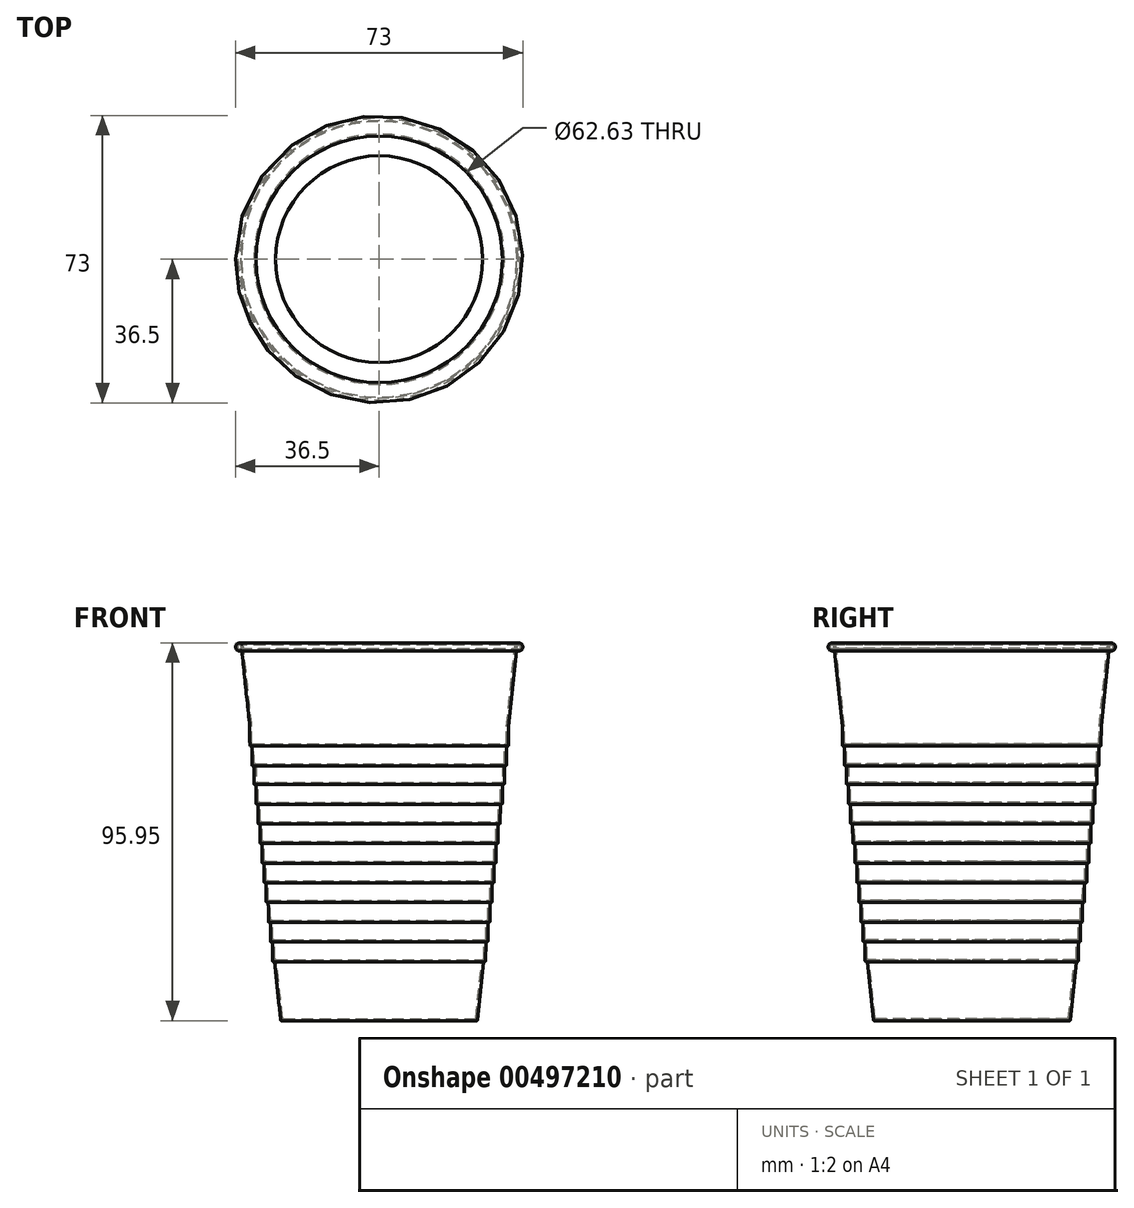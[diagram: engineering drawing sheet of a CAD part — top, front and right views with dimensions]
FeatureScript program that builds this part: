
annotation { "Feature Type Name" : "Feature", "Feature Type Description" : "" }
export const myFeature = defineFeature(function(context is Context, id is Id, definition is map)
    precondition{}
    {
        {
            var Q0;
            Q0=qCreatedBy(makeId("Front.planeOp"),FACE);
            var sketch = newSketch(context, id + "F0", { "sketchPlane" : qUnion([Q0])});
            skLineSegment(sketch, "E0", {"start": v(0, 0) * mm, "end": v(24.82, 0) * mm});
            skLineSegment(sketch, "E1", {"start": v(25.02, 0.18) * mm, "end": v(26.56, 14.82) * mm});
            skLineSegment(sketch, "E2", {"start": v(26.76, 15) * mm, "end": v(26.88, 15) * mm});
            skLineSegment(sketch, "E3", {"start": v(27.08, 15.2) * mm, "end": v(27.1, 19.8) * mm});
            skLineSegment(sketch, "E4", {"start": v(27.3, 20) * mm, "end": v(27.4, 20) * mm});
            skLineSegment(sketch, "E5", {"start": v(27.6, 20.2) * mm, "end": v(27.63, 24.8) * mm});
            skLineSegment(sketch, "E6", {"start": v(27.83, 25) * mm, "end": v(27.93, 25) * mm});
            skLineSegment(sketch, "E7", {"start": v(28.13, 25.2) * mm, "end": v(28.16, 29.8) * mm});
            skLineSegment(sketch, "E8", {"start": v(28.36, 30) * mm, "end": v(28.46, 30) * mm});
            skLineSegment(sketch, "E9", {"start": v(28.66, 30.2) * mm, "end": v(28.68, 34.8) * mm});
            skLineSegment(sketch, "E10", {"start": v(29.19, 35.2) * mm, "end": v(29.2, 39.8) * mm});
            skLineSegment(sketch, "E11", {"start": v(28.88, 35) * mm, "end": v(28.99, 35) * mm});
            skLineSegment(sketch, "E12", {"start": v(29.4, 40) * mm, "end": v(29.51, 40) * mm});
            skLineSegment(sketch, "E13", {"start": v(29.71, 40.2) * mm, "end": v(29.74, 44.8) * mm});
            skLineSegment(sketch, "E14", {"start": v(29.94, 45) * mm, "end": v(30.04, 45) * mm});
            skLineSegment(sketch, "E15", {"start": v(30.24, 45.2) * mm, "end": v(30.26, 49.8) * mm});
            skLineSegment(sketch, "E16", {"start": v(30.46, 50) * mm, "end": v(30.56, 50) * mm});
            skLineSegment(sketch, "E17", {"start": v(30.76, 50.2) * mm, "end": v(30.79, 54.8) * mm});
            skLineSegment(sketch, "E18", {"start": v(30.99, 55) * mm, "end": v(31.1, 55) * mm});
            skLineSegment(sketch, "E19", {"start": v(31.3, 55.2) * mm, "end": v(31.31, 59.8) * mm});
            skLineSegment(sketch, "E20", {"start": v(31.51, 60) * mm, "end": v(31.62, 60) * mm});
            skLineSegment(sketch, "E21", {"start": v(31.82, 60.2) * mm, "end": v(31.82, 64.55) * mm});
            skLineSegment(sketch, "E22", {"start": v(32.02, 64.75) * mm, "end": v(32.12, 64.75) * mm});
            skLineSegment(sketch, "E23", {"start": v(32.32, 64.95) * mm, "end": v(32.34, 69.55) * mm});
            skLineSegment(sketch, "E24", {"start": v(32.54, 69.75) * mm, "end": v(32.64, 69.75) * mm});
            skLineSegment(sketch, "E25", {"start": v(32.84, 69.95) * mm, "end": v(32.87, 74.74) * mm});
            skArc(sketch, "E26", {"start": v(35.25, 94.51) * mm, "mid": v(35.94, 95.17) * mm, "end": v(35, 95) * mm});
            skLineSegment(sketch, "E27", {"start": v(35.25, 94.51) * mm, "end": v(35.5, 94.95) * mm, "construction": true});
            skLineSegment(sketch, "E28", {"start": v(35.5, 94.95) * mm, "end": v(35.5, 94.45) * mm, "construction": true});
            skArc(sketch, "E29.0", {"start": v(35, 94.08) * mm, "mid": v(36.39, 95.4) * mm, "end": v(34.5, 95.05) * mm});
            skLineSegment(sketch, "E29.2", {"start": v(0, 0.5) * mm, "end": v(24.37, 0.5) * mm});
            skLineSegment(sketch, "E30", {"start": v(35, 94.08) * mm, "end": v(35.25, 94.51) * mm});
            skLineSegment(sketch, "E31", {"start": v(0, 0.5) * mm, "end": v(0, 0) * mm});
            skLineSegment(sketch, "E32", {"start": v(0, 0.5) * mm, "end": v(0, 74.17) * mm, "construction": true});
            skLineSegment(sketch, "E33.trimOffspring", {"start": v(32.87, 74.76) * mm, "end": v(35, 95) * mm});
            skLineSegment(sketch, "E34.0", {"start": v(32.35, 70.45) * mm, "end": v(32.37, 74.77) * mm});
            skLineSegment(sketch, "E34.1", {"start": v(32.04, 70.25) * mm, "end": v(32.15, 70.25) * mm});
            skLineSegment(sketch, "E34.2", {"start": v(31.82, 65.45) * mm, "end": v(31.84, 70.05) * mm});
            skLineSegment(sketch, "E34.3", {"start": v(31.52, 65.25) * mm, "end": v(31.62, 65.25) * mm});
            skLineSegment(sketch, "E34.4", {"start": v(31.32, 60.7) * mm, "end": v(31.32, 65.05) * mm});
            skLineSegment(sketch, "E34.5", {"start": v(31.02, 60.5) * mm, "end": v(31.12, 60.5) * mm});
            skLineSegment(sketch, "E34.6", {"start": v(30.8, 55.7) * mm, "end": v(30.82, 60.3) * mm});
            skLineSegment(sketch, "E34.7", {"start": v(30.5, 55.5) * mm, "end": v(30.6, 55.5) * mm});
            skLineSegment(sketch, "E34.8", {"start": v(30.27, 50.7) * mm, "end": v(30.3, 55.3) * mm});
            skLineSegment(sketch, "E34.9", {"start": v(29.96, 50.5) * mm, "end": v(30.07, 50.5) * mm});
            skLineSegment(sketch, "E34.10", {"start": v(29.74, 45.7) * mm, "end": v(29.76, 50.3) * mm});
            skLineSegment(sketch, "E34.11", {"start": v(29.44, 45.5) * mm, "end": v(29.54, 45.5) * mm});
            skLineSegment(sketch, "E34.12", {"start": v(27.64, 25.7) * mm, "end": v(27.66, 30.3) * mm});
            skLineSegment(sketch, "E34.13", {"start": v(27.33, 25.5) * mm, "end": v(27.44, 25.5) * mm});
            skLineSegment(sketch, "E34.14", {"start": v(27.1, 20.7) * mm, "end": v(27.13, 25.3) * mm});
            skLineSegment(sketch, "E34.15", {"start": v(26.8, 20.5) * mm, "end": v(26.9, 20.5) * mm});
            skLineSegment(sketch, "E34.16", {"start": v(27.86, 30.5) * mm, "end": v(27.96, 30.5) * mm});
            skLineSegment(sketch, "E34.17", {"start": v(28.16, 30.7) * mm, "end": v(28.19, 35.3) * mm});
            skLineSegment(sketch, "E34.18", {"start": v(28.39, 35.5) * mm, "end": v(28.49, 35.5) * mm});
            skLineSegment(sketch, "E34.19", {"start": v(28.69, 35.7) * mm, "end": v(28.71, 40.3) * mm});
            skLineSegment(sketch, "E34.20", {"start": v(28.91, 40.5) * mm, "end": v(29.01, 40.5) * mm});
            skLineSegment(sketch, "E34.21", {"start": v(29.21, 40.7) * mm, "end": v(29.24, 45.3) * mm});
            skLineSegment(sketch, "E35.0", {"start": v(26.58, 15.8) * mm, "end": v(26.6, 20.3) * mm});
            skLineSegment(sketch, "E35.1", {"start": v(26.28, 15.5) * mm, "end": v(26.3, 15.5) * mm});
            skLineSegment(sketch, "E35.2", {"start": v(24.57, 0.68) * mm, "end": v(26.1, 15.32) * mm});
            skLineSegment(sketch, "E36.0", {"start": v(32.37, 74.79) * mm, "end": v(34.5, 95.05) * mm});
            skPoint(sketch, "E37.visualSharp", {"position": v(26.58, 15) * mm});
            skArc(sketch, "E37.filletArc", {"start": v(26.76, 15) * mm, "mid": v(26.63, 14.95) * mm, "end": v(26.56, 14.82) * mm});
            skPoint(sketch, "E38.visualSharp", {"position": v(27.08, 15) * mm});
            skArc(sketch, "E38.filletArc", {"start": v(26.88, 15) * mm, "mid": v(27.02, 15.06) * mm, "end": v(27.08, 15.2) * mm});
            skPoint(sketch, "E39.visualSharp", {"position": v(26.13, 15.5) * mm});
            skArc(sketch, "E39.filletArc", {"start": v(26.3, 15.5) * mm, "mid": v(26.18, 15.45) * mm, "end": v(26.1, 15.32) * mm});
            skPoint(sketch, "E40.visualSharp", {"position": v(26.58, 15.5) * mm});
            skArc(sketch, "E40.filletArc", {"start": v(26.28, 15.5) * mm, "mid": v(26.5, 15.59) * mm, "end": v(26.58, 15.8) * mm});
            skPoint(sketch, "E41.visualSharp", {"position": v(26.6, 20.5) * mm});
            skArc(sketch, "E41.filletArc", {"start": v(26.8, 20.5) * mm, "mid": v(26.67, 20.44) * mm, "end": v(26.6, 20.3) * mm});
            skPoint(sketch, "E42.visualSharp", {"position": v(27.6, 20) * mm});
            skArc(sketch, "E42.filletArc", {"start": v(27.4, 20) * mm, "mid": v(27.55, 20.06) * mm, "end": v(27.6, 20.2) * mm});
            skPoint(sketch, "E43.visualSharp", {"position": v(27.1, 20) * mm});
            skArc(sketch, "E43.filletArc", {"start": v(27.3, 20) * mm, "mid": v(27.16, 19.94) * mm, "end": v(27.1, 19.8) * mm});
            skPoint(sketch, "E44.visualSharp", {"position": v(27.1, 20.5) * mm});
            skArc(sketch, "E44.filletArc", {"start": v(26.9, 20.5) * mm, "mid": v(27.05, 20.56) * mm, "end": v(27.1, 20.7) * mm});
            skPoint(sketch, "E45.visualSharp", {"position": v(27.13, 25.5) * mm});
            skArc(sketch, "E45.filletArc", {"start": v(27.33, 25.5) * mm, "mid": v(27.2, 25.44) * mm, "end": v(27.13, 25.3) * mm});
            skPoint(sketch, "E46.visualSharp", {"position": v(27.63, 25) * mm});
            skArc(sketch, "E46.filletArc", {"start": v(27.83, 25) * mm, "mid": v(27.69, 24.94) * mm, "end": v(27.63, 24.8) * mm});
            skPoint(sketch, "E47.visualSharp", {"position": v(27.63, 25.5) * mm});
            skArc(sketch, "E47.filletArc", {"start": v(27.44, 25.5) * mm, "mid": v(27.58, 25.56) * mm, "end": v(27.64, 25.7) * mm});
            skPoint(sketch, "E48.visualSharp", {"position": v(28.13, 25) * mm});
            skArc(sketch, "E48.filletArc", {"start": v(27.93, 25) * mm, "mid": v(28.07, 25.06) * mm, "end": v(28.13, 25.2) * mm});
            skPoint(sketch, "E49.visualSharp", {"position": v(27.66, 30.5) * mm});
            skArc(sketch, "E49.filletArc", {"start": v(27.86, 30.5) * mm, "mid": v(27.72, 30.44) * mm, "end": v(27.66, 30.3) * mm});
            skPoint(sketch, "E50.visualSharp", {"position": v(28.16, 30.5) * mm});
            skArc(sketch, "E50.filletArc", {"start": v(27.96, 30.5) * mm, "mid": v(28.1, 30.56) * mm, "end": v(28.16, 30.7) * mm});
            skPoint(sketch, "E51.visualSharp", {"position": v(28.66, 30) * mm});
            skArc(sketch, "E51.filletArc", {"start": v(28.46, 30) * mm, "mid": v(28.6, 30.06) * mm, "end": v(28.66, 30.2) * mm});
            skPoint(sketch, "E52.visualSharp", {"position": v(28.16, 30) * mm});
            skArc(sketch, "E52.filletArc", {"start": v(28.36, 30) * mm, "mid": v(28.22, 29.94) * mm, "end": v(28.16, 29.8) * mm});
            skPoint(sketch, "E53.visualSharp", {"position": v(28.19, 35.5) * mm});
            skArc(sketch, "E53.filletArc", {"start": v(28.39, 35.5) * mm, "mid": v(28.24, 35.44) * mm, "end": v(28.19, 35.3) * mm});
            skPoint(sketch, "E54.visualSharp", {"position": v(28.69, 35.5) * mm});
            skArc(sketch, "E54.filletArc", {"start": v(28.49, 35.5) * mm, "mid": v(28.63, 35.56) * mm, "end": v(28.69, 35.7) * mm});
            skPoint(sketch, "E55.visualSharp", {"position": v(28.68, 35) * mm});
            skArc(sketch, "E55.filletArc", {"start": v(28.88, 35) * mm, "mid": v(28.74, 34.94) * mm, "end": v(28.68, 34.8) * mm});
            skPoint(sketch, "E56.visualSharp", {"position": v(29.18, 35) * mm});
            skArc(sketch, "E56.filletArc", {"start": v(28.99, 35) * mm, "mid": v(29.13, 35.06) * mm, "end": v(29.19, 35.2) * mm});
            skPoint(sketch, "E57.visualSharp", {"position": v(28.71, 40.5) * mm});
            skArc(sketch, "E57.filletArc", {"start": v(28.91, 40.5) * mm, "mid": v(28.77, 40.44) * mm, "end": v(28.71, 40.3) * mm});
            skPoint(sketch, "E58.visualSharp", {"position": v(29.21, 40.5) * mm});
            skArc(sketch, "E58.filletArc", {"start": v(29.01, 40.5) * mm, "mid": v(29.16, 40.56) * mm, "end": v(29.21, 40.7) * mm});
            skPoint(sketch, "E59.visualSharp", {"position": v(29.71, 40) * mm});
            skArc(sketch, "E59.filletArc", {"start": v(29.51, 40) * mm, "mid": v(29.65, 40.06) * mm, "end": v(29.71, 40.2) * mm});
            skPoint(sketch, "E60.visualSharp", {"position": v(29.21, 40) * mm});
            skArc(sketch, "E60.filletArc", {"start": v(29.4, 40) * mm, "mid": v(29.27, 39.94) * mm, "end": v(29.2, 39.8) * mm});
            skPoint(sketch, "E61.visualSharp", {"position": v(29.24, 45.5) * mm});
            skArc(sketch, "E61.filletArc", {"start": v(29.44, 45.5) * mm, "mid": v(29.3, 45.44) * mm, "end": v(29.24, 45.3) * mm});
            skPoint(sketch, "E62.visualSharp", {"position": v(29.74, 45.5) * mm});
            skArc(sketch, "E62.filletArc", {"start": v(29.54, 45.5) * mm, "mid": v(29.68, 45.56) * mm, "end": v(29.74, 45.7) * mm});
            skPoint(sketch, "E63.visualSharp", {"position": v(29.74, 45) * mm});
            skArc(sketch, "E63.filletArc", {"start": v(29.94, 45) * mm, "mid": v(29.8, 44.94) * mm, "end": v(29.74, 44.8) * mm});
            skPoint(sketch, "E64.visualSharp", {"position": v(30.24, 45) * mm});
            skArc(sketch, "E64.filletArc", {"start": v(30.04, 45) * mm, "mid": v(30.18, 45.06) * mm, "end": v(30.24, 45.2) * mm});
            skPoint(sketch, "E65.visualSharp", {"position": v(29.77, 50.5) * mm});
            skArc(sketch, "E65.filletArc", {"start": v(29.96, 50.5) * mm, "mid": v(29.82, 50.44) * mm, "end": v(29.76, 50.3) * mm});
            skPoint(sketch, "E66.visualSharp", {"position": v(30.27, 50.5) * mm});
            skArc(sketch, "E66.filletArc", {"start": v(30.07, 50.5) * mm, "mid": v(30.2, 50.56) * mm, "end": v(30.27, 50.7) * mm});
            skPoint(sketch, "E67.visualSharp", {"position": v(30.76, 50) * mm});
            skArc(sketch, "E67.filletArc", {"start": v(30.56, 50) * mm, "mid": v(30.7, 50.06) * mm, "end": v(30.76, 50.2) * mm});
            skPoint(sketch, "E68.visualSharp", {"position": v(30.26, 50) * mm});
            skArc(sketch, "E68.filletArc", {"start": v(30.46, 50) * mm, "mid": v(30.32, 49.94) * mm, "end": v(30.26, 49.8) * mm});
            skPoint(sketch, "E69.visualSharp", {"position": v(31.29, 55) * mm});
            skArc(sketch, "E69.filletArc", {"start": v(31.1, 55) * mm, "mid": v(31.23, 55.06) * mm, "end": v(31.3, 55.2) * mm});
            skPoint(sketch, "E70.visualSharp", {"position": v(30.79, 55) * mm});
            skArc(sketch, "E70.filletArc", {"start": v(30.99, 55) * mm, "mid": v(30.85, 54.94) * mm, "end": v(30.79, 54.8) * mm});
            skPoint(sketch, "E71.visualSharp", {"position": v(30.8, 55.5) * mm});
            skArc(sketch, "E71.filletArc", {"start": v(30.6, 55.5) * mm, "mid": v(30.73, 55.56) * mm, "end": v(30.8, 55.7) * mm});
            skPoint(sketch, "E72.visualSharp", {"position": v(30.3, 55.5) * mm});
            skArc(sketch, "E72.filletArc", {"start": v(30.5, 55.5) * mm, "mid": v(30.35, 55.44) * mm, "end": v(30.3, 55.3) * mm});
            skPoint(sketch, "E73.visualSharp", {"position": v(31.32, 60.5) * mm});
            skArc(sketch, "E73.filletArc", {"start": v(31.12, 60.5) * mm, "mid": v(31.26, 60.56) * mm, "end": v(31.32, 60.7) * mm});
            skPoint(sketch, "E74.visualSharp", {"position": v(30.82, 60.5) * mm});
            skArc(sketch, "E74.filletArc", {"start": v(31.02, 60.5) * mm, "mid": v(30.88, 60.44) * mm, "end": v(30.82, 60.3) * mm});
            skPoint(sketch, "E75.visualSharp", {"position": v(31.32, 60) * mm});
            skArc(sketch, "E75.filletArc", {"start": v(31.51, 60) * mm, "mid": v(31.37, 59.94) * mm, "end": v(31.31, 59.8) * mm});
            skPoint(sketch, "E76.visualSharp", {"position": v(31.82, 60) * mm});
            skArc(sketch, "E76.filletArc", {"start": v(31.62, 60) * mm, "mid": v(31.76, 60.06) * mm, "end": v(31.82, 60.2) * mm});
            skPoint(sketch, "E77.visualSharp", {"position": v(31.84, 70.25) * mm});
            skArc(sketch, "E77.filletArc", {"start": v(32.04, 70.25) * mm, "mid": v(31.9, 70.2) * mm, "end": v(31.84, 70.05) * mm});
            skPoint(sketch, "E78.visualSharp", {"position": v(32.34, 70.25) * mm});
            skArc(sketch, "E78.filletArc", {"start": v(32.15, 70.25) * mm, "mid": v(32.29, 70.3) * mm, "end": v(32.35, 70.45) * mm});
            skPoint(sketch, "E79.visualSharp", {"position": v(32.84, 69.75) * mm});
            skArc(sketch, "E79.filletArc", {"start": v(32.64, 69.75) * mm, "mid": v(32.78, 69.8) * mm, "end": v(32.84, 69.95) * mm});
            skPoint(sketch, "E80.visualSharp", {"position": v(32.34, 69.75) * mm});
            skArc(sketch, "E80.filletArc", {"start": v(32.54, 69.75) * mm, "mid": v(32.4, 69.7) * mm, "end": v(32.34, 69.55) * mm});
            skPoint(sketch, "E81.visualSharp", {"position": v(32.32, 64.75) * mm});
            skArc(sketch, "E81.filletArc", {"start": v(32.12, 64.75) * mm, "mid": v(32.26, 64.8) * mm, "end": v(32.32, 64.95) * mm});
            skPoint(sketch, "E82.visualSharp", {"position": v(31.82, 64.75) * mm});
            skArc(sketch, "E82.filletArc", {"start": v(32.02, 64.75) * mm, "mid": v(31.87, 64.7) * mm, "end": v(31.82, 64.55) * mm});
            skPoint(sketch, "E83.visualSharp", {"position": v(31.32, 65.25) * mm});
            skArc(sketch, "E83.filletArc", {"start": v(31.52, 65.25) * mm, "mid": v(31.37, 65.2) * mm, "end": v(31.32, 65.05) * mm});
            skPoint(sketch, "E84.visualSharp", {"position": v(31.82, 65.25) * mm});
            skArc(sketch, "E84.filletArc", {"start": v(31.62, 65.25) * mm, "mid": v(31.76, 65.3) * mm, "end": v(31.82, 65.45) * mm});
            skPoint(sketch, "E85.visualSharp", {"position": v(32.87, 74.75) * mm});
            skArc(sketch, "E85.filletArc", {"start": v(32.87, 74.76) * mm, "mid": v(32.87, 74.75) * mm, "end": v(32.87, 74.74) * mm});
            skPoint(sketch, "E86.visualSharp", {"position": v(32.37, 74.78) * mm});
            skArc(sketch, "E86.filletArc", {"start": v(32.37, 74.79) * mm, "mid": v(32.37, 74.78) * mm, "end": v(32.37, 74.77) * mm});
            skPoint(sketch, "E87.visualSharp", {"position": v(24.55, 0.5) * mm});
            skArc(sketch, "E87.filletArc", {"start": v(24.37, 0.5) * mm, "mid": v(24.5, 0.55) * mm, "end": v(24.57, 0.68) * mm});
            skPoint(sketch, "E88.visualSharp", {"position": v(25, 0) * mm});
            skArc(sketch, "E88.filletArc", {"start": v(24.82, 0) * mm, "mid": v(24.95, 0.05) * mm, "end": v(25.02, 0.18) * mm});
            skSolve(sketch);
        }
        {
            var Q0;
            Q0=makeQuery(id+"F0.imprint","IMPRINT",FACE,{"disambiguationData":[TD([[makeQuery(id+"F0.imprint","IMPRINT",EDGE,{"derivedFrom":sQuery(id+"F0.wireOp",EDGE,"E0")}),1.0]])]});
            var Q1;
            Q1=sQuery(id+"F0.wireOp",EDGE,"E32");
            revolve(context, id + "F1", {"entities" : qUnion([Q0]), "axis" : qUnion([Q1]), "revolveType" : RevolveType.FULL});
        }
    });
